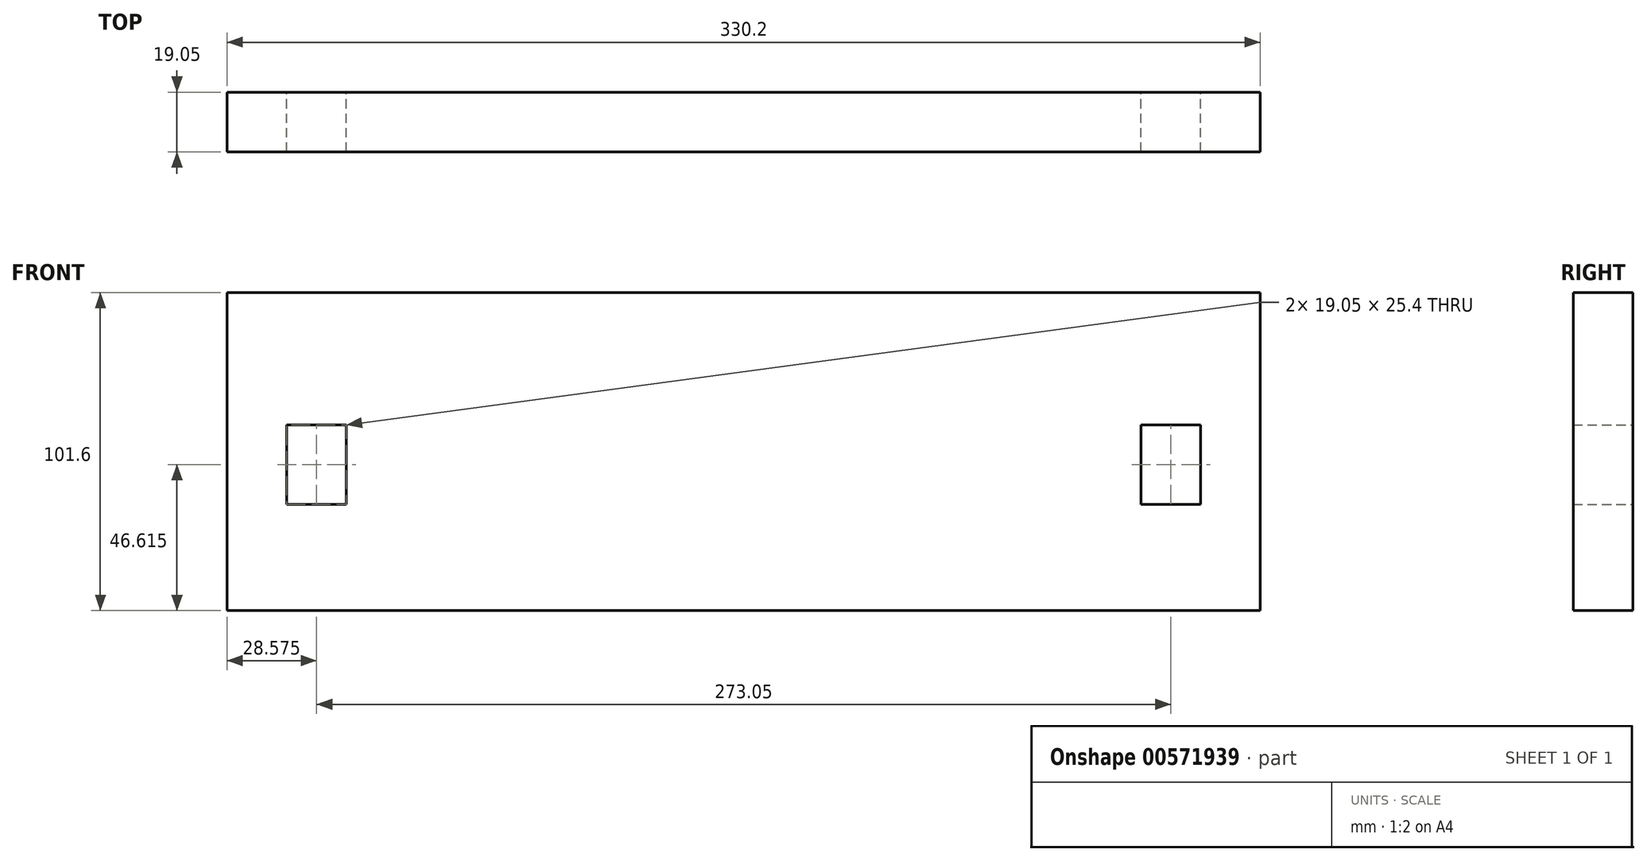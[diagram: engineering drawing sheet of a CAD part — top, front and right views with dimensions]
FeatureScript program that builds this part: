
annotation { "Feature Type Name" : "Feature", "Feature Type Description" : "" }
export const myFeature = defineFeature(function(context is Context, id is Id, definition is map)
    precondition{}
    {
        {
            var Q0;
            Q0=qCreatedBy(makeId("Front.planeOp"),FACE);
            var sketch = newSketch(context, id + "F0", { "sketchPlane" : qUnion([Q0])});
            skLineSegment(sketch, "E0.bottom", {"start": v(0, 0) * mm, "end": v(-330.2, 0) * mm});
            skLineSegment(sketch, "E0.top", {"start": v(0, 101.6) * mm, "end": v(-330.2, 101.6) * mm});
            skLineSegment(sketch, "E0.left", {"start": v(0, 0) * mm, "end": v(0, 101.6) * mm});
            skLineSegment(sketch, "E0.right", {"start": v(-330.2, 0) * mm, "end": v(-330.2, 101.6) * mm});
            skLineSegment(sketch, "E1", {"start": v(-311.15, 46.61) * mm, "end": v(-19.05, 46.61) * mm});
            skLineSegment(sketch, "E2.right", {"start": v(-311.15, 33.91) * mm, "end": v(-311.15, 59.31) * mm});
            skLineSegment(sketch, "E3.right", {"start": v(-19.05, 33.91) * mm, "end": v(-19.05, 59.31) * mm});
            skLineSegment(sketch, "E4.bottom", {"start": v(-311.15, 59.31) * mm, "end": v(-292.1, 59.31) * mm});
            skLineSegment(sketch, "E4.top", {"start": v(-311.15, 33.91) * mm, "end": v(-292.1, 33.91) * mm});
            skLineSegment(sketch, "E4.left", {"start": v(-311.15, 59.31) * mm, "end": v(-311.15, 33.91) * mm});
            skLineSegment(sketch, "E4.right", {"start": v(-292.1, 59.31) * mm, "end": v(-292.1, 33.91) * mm});
            skLineSegment(sketch, "E5.bottom", {"start": v(-19.05, 59.31) * mm, "end": v(-38.1, 59.31) * mm});
            skLineSegment(sketch, "E5.top", {"start": v(-19.05, 33.91) * mm, "end": v(-38.1, 33.91) * mm});
            skLineSegment(sketch, "E5.left", {"start": v(-19.05, 59.31) * mm, "end": v(-19.05, 33.91) * mm});
            skLineSegment(sketch, "E5.right", {"start": v(-38.1, 59.31) * mm, "end": v(-38.1, 33.91) * mm});
            skSolve(sketch);
        }
        {
            var Q0;
            Q0 = qSketchRegion(id + "F0", true);
            extrude(context, id + "F1", {"entities" : qUnion([Q0]), "depth" : 19.05 * mm, "offsetDistance" : 25.4 * mm});
        }
    });
